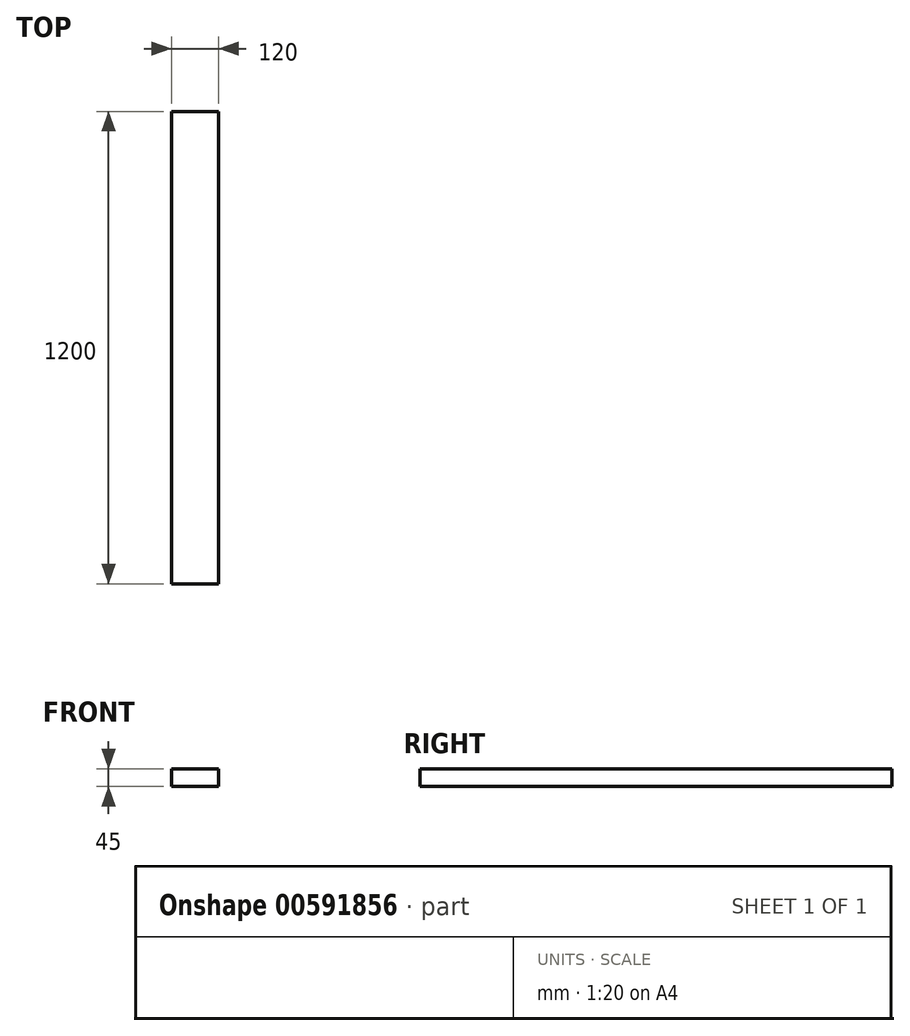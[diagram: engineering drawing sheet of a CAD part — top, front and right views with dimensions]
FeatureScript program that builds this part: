
annotation { "Feature Type Name" : "Feature", "Feature Type Description" : "" }
export const myFeature = defineFeature(function(context is Context, id is Id, definition is map)
    precondition{}
    {
        {
            var Q0;
            Q0=qCreatedBy(makeId("Top.planeOp"),FACE);
            var sketch = newSketch(context, id + "F0", { "sketchPlane" : qUnion([Q0])});
            skLineSegment(sketch, "E0.bottom", {"start": v(0, 0) * mm, "end": v(-120, 0) * mm});
            skLineSegment(sketch, "E0.top", {"start": v(0, 1200) * mm, "end": v(-120, 1200) * mm});
            skLineSegment(sketch, "E0.left", {"start": v(0, 0) * mm, "end": v(0, 1200) * mm});
            skLineSegment(sketch, "E0.right", {"start": v(-120, 0) * mm, "end": v(-120, 1200) * mm});
            skSolve(sketch);
        }
        {
            var Q0;
            Q0=makeQuery(id+"F0.imprint","IMPRINT",FACE,{"disambiguationData":[TD([[makeQuery(id+"F0.imprint","IMPRINT",EDGE,{"derivedFrom":sQuery(id+"F0.wireOp",EDGE,"E0.bottom")}),-1.0]])]});
            extrude(context, id + "F1", {"entities" : qUnion([Q0]), "depth" : 45 * mm, "offsetDistance" : 25 * mm});
        }
    });
